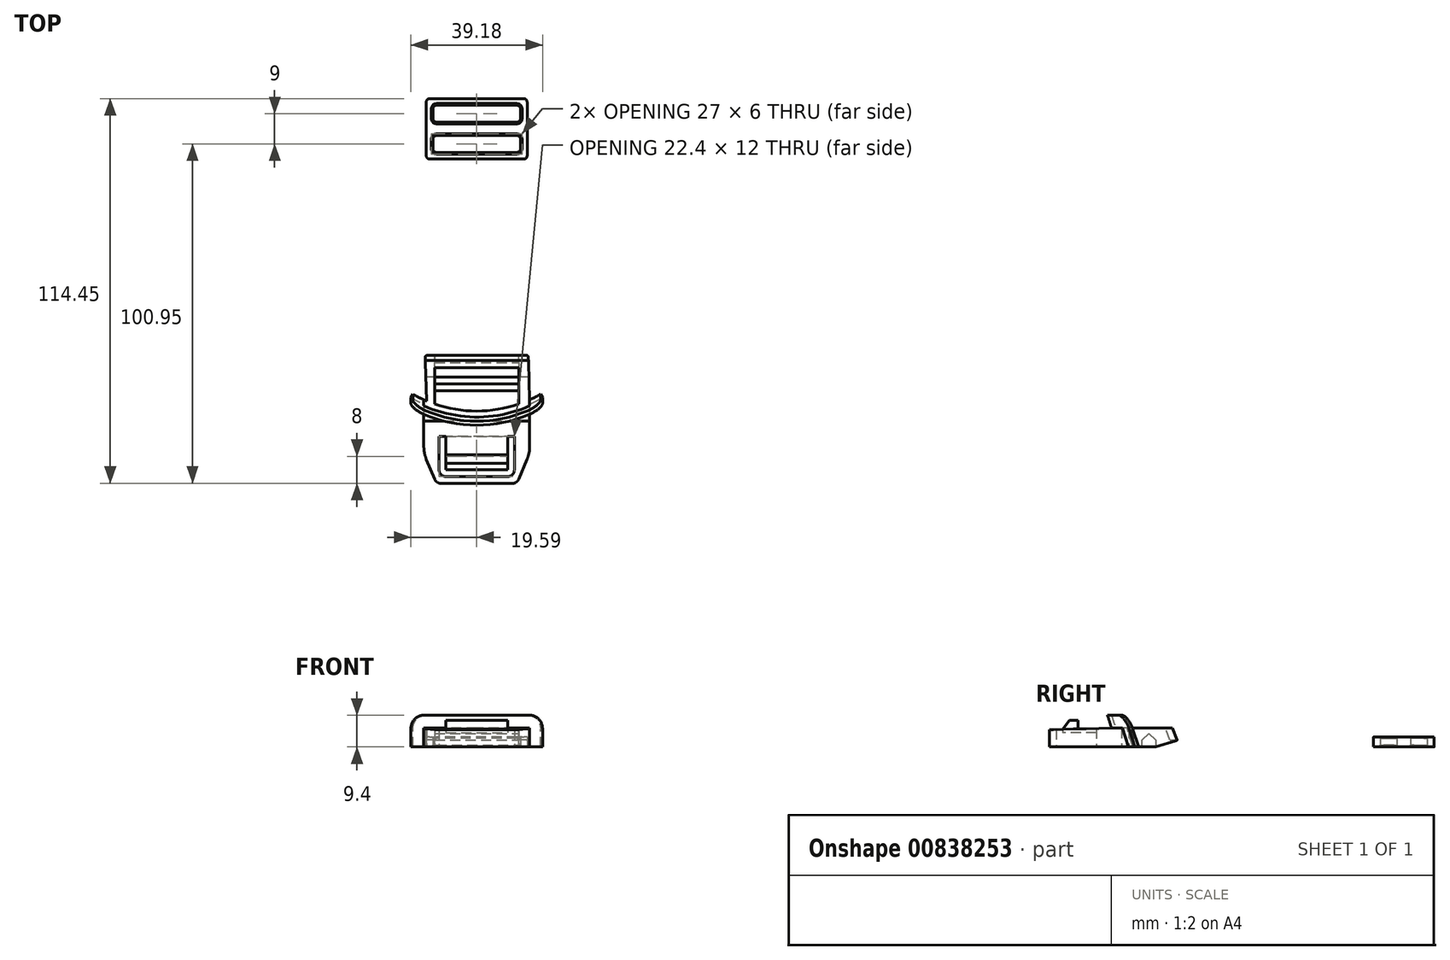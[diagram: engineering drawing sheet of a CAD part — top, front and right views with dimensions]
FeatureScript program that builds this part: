
annotation { "Feature Type Name" : "Feature", "Feature Type Description" : "" }
export const myFeature = defineFeature(function(context is Context, id is Id, definition is map)
    precondition{}
    {
        {
            var Q0;
            Q0=qCreatedBy(makeId("Top.planeOp"),FACE);
            var sketch = newSketch(context, id + "F0", { "sketchPlane" : qUnion([Q0])});
            skArc(sketch, "E0", {"start": v(-19, 0) * mm, "mid": v(0, -5) * mm, "end": v(19, 0) * mm});
            skLineSegment(sketch, "E1", {"start": v(0, 0) * mm, "end": v(0, -22.21) * mm, "construction": true});
            skLineSegment(sketch, "E2", {"start": v(-19, 0) * mm, "end": v(-19.6, -1.04) * mm});
            skArc(sketch, "E3", {"start": v(-19.6, -1.04) * mm, "mid": v(0, -6.2) * mm, "end": v(19.6, -1.04) * mm});
            skLineSegment(sketch, "E4", {"start": v(19, 0) * mm, "end": v(19.6, -1.04) * mm});
            skSolve(sketch);
        }
        {
            var Q0;
            Q0=qCreatedBy(makeId("Right.planeOp"),FACE);
            var sketch = newSketch(context, id + "F1", { "sketchPlane" : qUnion([Q0])});
            skLineSegment(sketch, "E5", {"start": v(-5, 0) * mm, "end": v(-8, 9.4) * mm});
            skSolve(sketch);
        }
        {
            var Q0;
            Q0=makeQuery(id+"F0.imprint","IMPRINT",FACE,{"disambiguationData":[TD([[makeQuery(id+"F0.imprint","IMPRINT",EDGE,{"derivedFrom":sQuery(id+"F0.wireOp",EDGE,"E0")}),-1.0]])]});
            var Q1;
            Q1=sQuery(id+"F1.wireOp",EDGE,"E5");
            sweep(context, id + "F2", {"profiles" : qUnion([Q0]), "path" : qUnion([Q1])});
        }
        {
            var Q0;
            Q0=qCreatedBy(makeId("Top.planeOp"),FACE);
            var sketch = newSketch(context, id + "F3", { "sketchPlane" : qUnion([Q0])});
            skLineSegment(sketch, "E6", {"start": v(-12, -26.5) * mm, "end": v(12, -26.5) * mm});
            skLineSegment(sketch, "E7", {"start": v(0, 0) * mm, "end": v(0, -12.9) * mm, "construction": true});
            skLineSegment(sketch, "E8", {"start": v(-15.75, -1.64) * mm, "end": v(-15.75, -17.5) * mm});
            skLineSegment(sketch, "E9", {"start": v(-15.75, -17.5) * mm, "end": v(-12, -26.5) * mm});
            skLineSegment(sketch, "E10.MirrorCS", {"start": v(15.75, -17.5) * mm, "end": v(12, -26.5) * mm});
            skLineSegment(sketch, "E11.MirrorCS", {"start": v(15.75, -1.64) * mm, "end": v(15.75, -17.5) * mm});
            skLineSegment(sketch, "E12", {"start": v(-11.2, -24.5) * mm, "end": v(-11.2, -12.5) * mm});
            skLineSegment(sketch, "E13", {"start": v(-11.2, -12.5) * mm, "end": v(-9.2, -12.5) * mm});
            skLineSegment(sketch, "E14", {"start": v(-9.2, -12.5) * mm, "end": v(-9.2, -22.5) * mm});
            skLineSegment(sketch, "E15", {"start": v(-9.2, -22.5) * mm, "end": v(9.2, -22.5) * mm});
            skLineSegment(sketch, "E16", {"start": v(-11.2, -24.5) * mm, "end": v(11.2, -24.5) * mm});
            skLineSegment(sketch, "E17.MirrorCS", {"start": v(11.2, -24.5) * mm, "end": v(11.2, -12.5) * mm});
            skLineSegment(sketch, "E18.MirrorCS", {"start": v(9.2, -12.5) * mm, "end": v(9.2, -22.5) * mm});
            skLineSegment(sketch, "E19.MirrorCS", {"start": v(11.2, -12.5) * mm, "end": v(9.2, -12.5) * mm});
            skArc(sketch, "E20.0", {"start": v(19, 0) * mm, "mid": v(0, -5) * mm, "end": v(-19, 0) * mm});
            skSolve(sketch);
        }
        {
            var Q0;
            Q0=makeQuery(id+"F3.imprint","IMPRINT",FACE,{"disambiguationData":[TD([[makeQuery(id+"F3.imprint","IMPRINT",EDGE,{"derivedFrom":sQuery(id+"F3.wireOp",EDGE,"E6")}),1.0]])]});
            extrude(context, id + "F4", {"entities" : qUnion([Q0]), "operationType" : NewBodyOperationType.ADD, "depth" : 5.6 * mm, "offsetDistance" : 25 * mm});
        }
        {
            var Q0;
            Q0=qCreatedBy(makeId("Right.planeOp"),FACE);
            var sketch = newSketch(context, id + "F5", { "sketchPlane" : qUnion([Q0])});
            skLineSegment(sketch, "E21", {"start": v(-7.99, 5.6) * mm, "end": v(-26.52, 5.1) * mm});
            skLineSegment(sketch, "E22", {"start": v(-26.5, 0) * mm, "end": v(-26.5, 5.6) * mm});
            skLineSegment(sketch, "E23", {"start": v(-26.5, 5.6) * mm, "end": v(-7.99, 5.6) * mm});
            skSolve(sketch);
        }
        {
            var Q0;
            {var subQ0=sQuery(id+"F5.wireOp",EDGE,"E23");Q0=makeQuery(id+"F5.imprint","IMPRINT",FACE,{"disambiguationData":[TD([[makeQuery(id+"F5.imprint","IMPRINT",EDGE,{"derivedFrom":subQ0}),-1.0]])]});}
            extrude(context, id + "F6", {"entities" : qUnion([Q0]), "operationType" : NewBodyOperationType.REMOVE, "endBound" : BoundingType.THROUGH_ALL, "oppositeDirection" : true, "depth" : 25 * mm, "offsetDistance" : 25 * mm, "hasSecondDirection" : true, "secondDirectionBound" : BoundingType.THROUGH_ALL, "secondDirectionOppositeDirection" : false, "secondDirectionDepth" : 25 * mm});
        }
        {
            var Q0;
            Q0=qCreatedBy(makeId("Right.planeOp"),FACE);
            var sketch = newSketch(context, id + "F7", { "sketchPlane" : qUnion([Q0])});
            skLineSegment(sketch, "E24", {"start": v(-22.5, 5.2) * mm, "end": v(-20.5, 7.86) * mm});
            skLineSegment(sketch, "E25", {"start": v(-20.5, 7.86) * mm, "end": v(-18, 7.93) * mm});
            skLineSegment(sketch, "E26", {"start": v(-18, 7.93) * mm, "end": v(-18, 5.33) * mm});
            skLineSegment(sketch, "E27", {"start": v(-18, 5.33) * mm, "end": v(-22.5, 5.2) * mm});
            skSolve(sketch);
        }
        {
            var Q0;
            Q0=makeQuery(id+"F7.imprint","IMPRINT",FACE,{"disambiguationData":[TD([[makeQuery(id+"F7.imprint","IMPRINT",EDGE,{"derivedFrom":sQuery(id+"F7.wireOp",EDGE,"E24")}),-1.0]])]});
            var Q1;
            Q1=makeQuery(id+"F4.opExtrude","SWEPT_FACE",FACE,{"disambiguationData":[OSD([sQuery(id+"F3.wireOp",EDGE,"E14")])]});
            var Q2;
            Q2=makeQuery(id+"F4.opExtrude","SWEPT_FACE",FACE,{"disambiguationData":[OSD([sQuery(id+"F3.wireOp",EDGE,"E18.MirrorCS")])]});
            extrude(context, id + "F8", {"entities" : qUnion([Q0]), "operationType" : NewBodyOperationType.ADD, "endBound" : BoundingType.UP_TO_SURFACE, "oppositeDirection" : true, "depth" : 25 * mm, "endBoundEntityFace" : qUnion([Q1]), "offsetDistance" : 25 * mm, "hasSecondDirection" : true, "secondDirectionBound" : BoundingType.UP_TO_SURFACE, "secondDirectionOppositeDirection" : false, "secondDirectionDepth" : 25 * mm, "secondDirectionBoundEntityFace" : qUnion([Q2])});
        }
        {
            var Q0;
            Q0=makeQuery(id+"F4.boolean.opBoolean","MERGE",FACE,{"derivedFrom":[makeQuery(id+"F2.opSweep","CAP_FACE",FACE,{"disambiguationData":[OSD([sQuery(id+"F0.wireOp",EDGE,"E0"),sQuery(id+"F0.wireOp",EDGE,"E2"),sQuery(id+"F0.wireOp",EDGE,"E3"),sQuery(id+"F0.wireOp",EDGE,"E4"),sQuery(id+"F1.wireOp",VERTEX,"E5.start")])],"isStart":true}),makeQuery(id+"F4.opExtrude","CAP_FACE",FACE,{"disambiguationData":[OSD([sQuery(id+"F3.wireOp",EDGE,"E6"),sQuery(id+"F3.wireOp",EDGE,"E8"),sQuery(id+"F3.wireOp",EDGE,"E9"),sQuery(id+"F3.wireOp",EDGE,"E10.MirrorCS"),sQuery(id+"F3.wireOp",EDGE,"E11.MirrorCS"),sQuery(id+"F3.wireOp",EDGE,"E12"),sQuery(id+"F3.wireOp",EDGE,"E13"),sQuery(id+"F3.wireOp",EDGE,"E14"),sQuery(id+"F3.wireOp",EDGE,"E15"),sQuery(id+"F3.wireOp",EDGE,"E16"),sQuery(id+"F3.wireOp",EDGE,"E17.MirrorCS"),sQuery(id+"F3.wireOp",EDGE,"E18.MirrorCS"),sQuery(id+"F3.wireOp",EDGE,"E19.MirrorCS"),sQuery(id+"F3.wireOp",EDGE,"E20.0")])],"isStart":true})]});
            var sketch = newSketch(context, id + "F9", { "sketchPlane" : qUnion([Q0])});
            skLineSegment(sketch, "E28", {"start": v(-9.2, 12.5) * mm, "end": v(9.2, 12.5) * mm});
            skSolve(sketch);
        }
        {
            var Q0;
            Q0=makeQuery(id+"F4.opExtrude","SWEPT_FACE",FACE,{"disambiguationData":[OSD([sQuery(id+"F3.wireOp",EDGE,"E15")])]});
            var sketch = newSketch(context, id + "F10", { "sketchPlane" : qUnion([Q0])});
            skPoint(sketch, "E29", {"position": v(-9.2, 4.2) * mm});
            skSolve(sketch);
        }
        {
            var Q0;
            Q0=makeQuery(id+"F9.imprint","IMPRINT",FACE,{"disambiguationData":[TD([[makeQuery(id+"F9.imprint","IMPRINT",EDGE,{"derivedFrom":sQuery(id+"F9.wireOp",EDGE,"E28")}),1.0]])]});
            var Q1;
            Q1=sQuery(id+"F10.wireOp",VERTEX,"E29");
            extrude(context, id + "F11", {"entities" : qUnion([Q0]), "operationType" : NewBodyOperationType.REMOVE, "endBound" : BoundingType.UP_TO_VERTEX, "oppositeDirection" : true, "depth" : 25 * mm, "endBoundEntityVertex" : qUnion([Q1]), "offsetDistance" : 25 * mm});
        }
        {
            var Q0;
            Q0=qCreatedBy(makeId("Top.planeOp"),FACE);
            var sketch = newSketch(context, id + "F12", { "sketchPlane" : qUnion([Q0])});
            skLineSegment(sketch, "E30.bottom", {"start": v(-12.5, 12.04) * mm, "end": v(12.5, 12.04) * mm});
            skLineSegment(sketch, "E30.left", {"start": v(-12.5, 12.04) * mm, "end": v(-12.5, -2.95) * mm});
            skLineSegment(sketch, "E30.right", {"start": v(12.5, 12.04) * mm, "end": v(12.5, -2.95) * mm});
            skLineSegment(sketch, "E31.bottom", {"start": v(-15.32, 12.04) * mm, "end": v(15.32, 12.04) * mm});
            skLineSegment(sketch, "E31.top", {"start": v(-14.9, -2.95) * mm, "end": v(15.75, -2.95) * mm});
            skLineSegment(sketch, "E31.left", {"start": v(-15.32, 12.04) * mm, "end": v(-14.9, -2.95) * mm});
            skLineSegment(sketch, "E31.right", {"start": v(15.32, 12.04) * mm, "end": v(15.75, -2.95) * mm});
            skSolve(sketch);
        }
        {
            var Q0;
            {var subQ0=sQuery(id+"F12.wireOp",EDGE,"E30.left");Q0=makeQuery(id+"F12.imprint","IMPRINT",FACE,{"disambiguationData":[TD([[makeQuery(id+"F12.imprint","IMPRINT",EDGE,{"derivedFrom":subQ0}),-1.0]])]});}
            var Q1;
            {var subQ0=sQuery(id+"F12.wireOp",EDGE,"E30.right");Q1=makeQuery(id+"F12.imprint","IMPRINT",FACE,{"disambiguationData":[TD([[makeQuery(id+"F12.imprint","IMPRINT",EDGE,{"derivedFrom":subQ0}),1.0]])]});}
            var Q2;
            {var subQ0=sQuery(id+"F3.wireOp",EDGE,"E8");var subQ1=sQuery(id+"F3.wireOp",EDGE,"E11.MirrorCS");var subQ2=sQuery(id+"F3.wireOp",EDGE,"E20.0");Q2=makeQuery(id+"F4.boolean.opBoolean","SPLIT",FACE,{"disambiguationData":[TD([makeQuery(id+"F4.opExtrude","SWEPT_FACE",FACE,{"disambiguationData":[OSD([subQ2])]})])],"derivedFrom":makeQuery(id+"F4.opExtrude","CAP_FACE",FACE,{"disambiguationData":[OSD([sQuery(id+"F3.wireOp",EDGE,"E6"),subQ0,sQuery(id+"F3.wireOp",EDGE,"E9"),sQuery(id+"F3.wireOp",EDGE,"E10.MirrorCS"),subQ1,sQuery(id+"F3.wireOp",EDGE,"E12"),sQuery(id+"F3.wireOp",EDGE,"E13"),sQuery(id+"F3.wireOp",EDGE,"E14"),sQuery(id+"F3.wireOp",EDGE,"E15"),sQuery(id+"F3.wireOp",EDGE,"E16"),sQuery(id+"F3.wireOp",EDGE,"E17.MirrorCS"),sQuery(id+"F3.wireOp",EDGE,"E18.MirrorCS"),sQuery(id+"F3.wireOp",EDGE,"E19.MirrorCS"),subQ2])],"isStart":false})});}
            extrude(context, id + "F13", {"entities" : qUnion([Q0, Q1]), "operationType" : NewBodyOperationType.ADD, "endBound" : BoundingType.UP_TO_SURFACE, "depth" : 25 * mm, "endBoundEntityFace" : qUnion([Q2]), "offsetDistance" : 25 * mm});
        }
        {
            var Q0;
            Q0=makeQuery(id+"F13.opExtrude","SWEPT_FACE",FACE,{"disambiguationData":[OSD([sQuery(id+"F12.wireOp",EDGE,"E30.right")])]});
            var sketch = newSketch(context, id + "F14", { "sketchPlane" : qUnion([Q0])});
            skLineSegment(sketch, "E32", {"start": v(-1.08, 0) * mm, "end": v(-1.08, 2) * mm});
            skLineSegment(sketch, "E33", {"start": v(-1.08, 2) * mm, "end": v(-3.08, 4) * mm});
            skLineSegment(sketch, "E34", {"start": v(-3.08, 4) * mm, "end": v(-5.08, 2) * mm});
            skLineSegment(sketch, "E35", {"start": v(-5.08, 2) * mm, "end": v(-5.08, 0) * mm});
            skLineSegment(sketch, "E36", {"start": v(-3.08, 0) * mm, "end": v(-3.08, 4) * mm, "construction": true});
            skLineSegment(sketch, "E37", {"start": v(-9.4, 2) * mm, "end": v(-7.94, 5.6) * mm});
            skLineSegment(sketch, "E38", {"start": v(-7.94, 5.6) * mm, "end": v(-10.1, 5.6) * mm});
            skLineSegment(sketch, "E39", {"start": v(-10.1, 5.6) * mm, "end": v(-11.55, 2) * mm});
            skLineSegment(sketch, "E40", {"start": v(-9.4, 2) * mm, "end": v(-11.55, 2) * mm});
            skLineSegment(sketch, "E41", {"start": v(-11.55, 2) * mm, "end": v(-5.08, 0) * mm});
            skSolve(sketch);
        }
        {
            var Q0;
            {var subQ1=sQuery(id+"F14.wireOp",EDGE,"E32");Q0=makeQuery(id+"F14.imprint","IMPRINT",FACE,{"disambiguationData":[TD([[makeQuery(id+"F14.imprint","IMPRINT",EDGE,{"derivedFrom":subQ1}),1.0]])]});}
            var Q1;
            {var subQ0=sQuery(id+"F14.wireOp",EDGE,"E37");Q1=makeQuery(id+"F14.imprint","IMPRINT",FACE,{"disambiguationData":[TD([[makeQuery(id+"F14.imprint","IMPRINT",EDGE,{"derivedFrom":subQ0}),1.0]])]});}
            var Q2;
            Q2=makeQuery(id+"F13.opExtrude","SWEPT_FACE",FACE,{"disambiguationData":[OSD([sQuery(id+"F12.wireOp",EDGE,"E30.left")])]});
            extrude(context, id + "F15", {"entities" : qUnion([Q0, Q1]), "operationType" : NewBodyOperationType.ADD, "endBound" : BoundingType.UP_TO_SURFACE, "depth" : 25 * mm, "endBoundEntityFace" : qUnion([Q2]), "offsetDistance" : 25 * mm});
        }
        {
            var Q0;
            {var subQ4=sQuery(id+"F14.wireOp",EDGE,"E39");Q0=makeQuery(id+"F14.imprint","IMPRINT",FACE,{"disambiguationData":[TD([[makeQuery(id+"F14.imprint","IMPRINT",EDGE,{"derivedFrom":subQ4}),-1.0]])]});}
            extrude(context, id + "F16", {"entities" : qUnion([Q0]), "operationType" : NewBodyOperationType.REMOVE, "endBound" : BoundingType.THROUGH_ALL, "oppositeDirection" : true, "depth" : 25 * mm, "offsetDistance" : 25 * mm, "hasSecondDirection" : true, "secondDirectionBound" : BoundingType.THROUGH_ALL, "secondDirectionOppositeDirection" : false, "secondDirectionDepth" : 25 * mm});
        }
        {
            var Q0;
            Q0=makeQuery(id+"F4.opExtrude","SWEPT_EDGE",EDGE,{"disambiguationData":[OSD([sQuery(id+"F3.wireOp",EDGE,"E12"),sQuery(id+"F3.wireOp",EDGE,"E16")])]});
            var Q1;
            Q1=makeQuery(id+"F4.opExtrude","SWEPT_EDGE",EDGE,{"disambiguationData":[OSD([sQuery(id+"F3.wireOp",EDGE,"E16"),sQuery(id+"F3.wireOp",EDGE,"E17.MirrorCS")])]});
            var Q2;
            Q2=makeQuery(id+"F4.opExtrude","SWEPT_EDGE",EDGE,{"disambiguationData":[OSD([sQuery(id+"F3.wireOp",EDGE,"E6"),sQuery(id+"F3.wireOp",EDGE,"E9")])]});
            var Q3;
            Q3=makeQuery(id+"F4.opExtrude","SWEPT_EDGE",EDGE,{"disambiguationData":[OSD([sQuery(id+"F3.wireOp",EDGE,"E6"),sQuery(id+"F3.wireOp",EDGE,"E10.MirrorCS")])]});
            fillet(context, id + "F17", {"entities" : qUnion([Q0, Q1, Q2, Q3]), "radius" : 2 * mm, "tangentPropagation" : true, "allowEdgeOverflow" : false});
        }
        {
            var Q0;
            Q0=makeQuery(id+"F4.opExtrude","SWEPT_EDGE",EDGE,{"disambiguationData":[OSD([sQuery(id+"F3.wireOp",EDGE,"E10.MirrorCS"),sQuery(id+"F3.wireOp",EDGE,"E11.MirrorCS")])]});
            var Q1;
            Q1=makeQuery(id+"F4.opExtrude","SWEPT_EDGE",EDGE,{"disambiguationData":[OSD([sQuery(id+"F3.wireOp",EDGE,"E8"),sQuery(id+"F3.wireOp",EDGE,"E9")])]});
            fillet(context, id + "F18", {"entities" : qUnion([Q0, Q1]), "radius" : 10 * mm, "tangentPropagation" : true, "allowEdgeOverflow" : false});
        }
        {
            var Q0;
            Q0=makeQuery(id+"F2.opSweep","CAP_EDGE",EDGE,{"disambiguationData":[OSD([sQuery(id+"F0.wireOp",EDGE,"E2"),sQuery(id+"F1.wireOp",VERTEX,"E5.end")])],"isStart":false});
            var Q1;
            Q1=makeQuery(id+"F2.opSweep","CAP_EDGE",EDGE,{"disambiguationData":[OSD([sQuery(id+"F0.wireOp",EDGE,"E4"),sQuery(id+"F1.wireOp",VERTEX,"E5.end")])],"isStart":false});
            fillet(context, id + "F19", {"entities" : qUnion([Q0, Q1]), "radius" : 5 * mm, "tangentPropagation" : true, "allowEdgeOverflow" : false});
        }
        {
            var Q0;
            Q0=makeQuery(id+"F16.boolean.opBoolean","INTERSECT",EDGE,{"derivedFrom":[makeQuery(id+"F13.opExtrude","SWEPT_FACE",FACE,{"disambiguationData":[OSD([sQuery(id+"F12.wireOp",EDGE,"E31.left")])]}),makeQuery(id+"F16.opExtrude","SWEPT_FACE",FACE,{"disambiguationData":[OSD([sQuery(id+"F14.wireOp",EDGE,"E39")])]})]});
            var Q1;
            Q1=makeQuery(id+"F16.boolean.opBoolean","INTERSECT",EDGE,{"derivedFrom":[makeQuery(id+"F13.opExtrude","SWEPT_FACE",FACE,{"disambiguationData":[OSD([sQuery(id+"F12.wireOp",EDGE,"E31.right")])]}),makeQuery(id+"F16.opExtrude","SWEPT_FACE",FACE,{"disambiguationData":[OSD([sQuery(id+"F14.wireOp",EDGE,"E39")])]})]});
            var Q2;
            Q2=makeQuery(id+"F15.opExtrude","TWEAK_EDGE",EDGE,{"derivedFrom":[makeQuery(id+"F13.opExtrude","SWEPT_FACE",FACE,{"disambiguationData":[OSD([sQuery(id+"F12.wireOp",EDGE,"E30.left")])]}),makeQuery(id+"F14.imprint","IMPRINT",EDGE,{"derivedFrom":sQuery(id+"F14.wireOp",EDGE,"E37")})]});
            fillet(context, id + "F20", {"entities" : qUnion([Q0, Q1, Q2]), "radius" : 0.5 * mm, "tangentPropagation" : true, "allowEdgeOverflow" : false});
        }
        {
            var Q0;
            Q0=qCreatedBy(makeId("Top.planeOp"),FACE);
            var sketch = newSketch(context, id + "F21", { "sketchPlane" : qUnion([Q0])});
            skLineSegment(sketch, "E42.bottom", {"start": v(-15, 87.95) * mm, "end": v(15, 87.95) * mm});
            skLineSegment(sketch, "E42.top", {"start": v(-15, 69.95) * mm, "end": v(15, 69.95) * mm});
            skLineSegment(sketch, "E42.left", {"start": v(-15, 87.95) * mm, "end": v(-15, 69.95) * mm});
            skLineSegment(sketch, "E42.right", {"start": v(15, 87.95) * mm, "end": v(15, 69.95) * mm});
            skPoint(sketch, "E42.middle", {"position": v(0, 78.95) * mm});
            skLineSegment(sketch, "E43.bottom", {"start": v(-13, 85.95) * mm, "end": v(13, 85.95) * mm});
            skLineSegment(sketch, "E43.top", {"start": v(-13, 80.95) * mm, "end": v(13, 80.95) * mm});
            skLineSegment(sketch, "E43.left", {"start": v(-13, 85.95) * mm, "end": v(-13, 80.95) * mm});
            skLineSegment(sketch, "E43.right", {"start": v(13, 85.95) * mm, "end": v(13, 80.95) * mm});
            skPoint(sketch, "E43.middle", {"position": v(0, 83.45) * mm});
            skLineSegment(sketch, "E44", {"start": v(-15, 78.95) * mm, "end": v(15, 78.95) * mm, "construction": true});
            skLineSegment(sketch, "E45.MirrorCS", {"start": v(-13, 71.95) * mm, "end": v(13, 71.95) * mm});
            skLineSegment(sketch, "E46.MirrorCS", {"start": v(-13, 76.95) * mm, "end": v(13, 76.95) * mm});
            skLineSegment(sketch, "E47.MirrorCS", {"start": v(13, 71.95) * mm, "end": v(13, 76.95) * mm});
            skLineSegment(sketch, "E48.MirrorCS", {"start": v(-13, 71.95) * mm, "end": v(-13, 76.95) * mm});
            skSolve(sketch);
        }
        {
            var Q0;
            Q0=makeQuery(id+"F21.imprint","IMPRINT",FACE,{"disambiguationData":[TD([[makeQuery(id+"F21.imprint","IMPRINT",EDGE,{"derivedFrom":sQuery(id+"F21.wireOp",EDGE,"E42.bottom")}),-1.0]])]});
            extrude(context, id + "F22", {"entities" : qUnion([Q0]), "depth" : 3 * mm, "offsetDistance" : 25 * mm});
        }
        {
            var Q0;
            Q0=makeQuery(id+"F22.opExtrude","SWEPT_EDGE",EDGE,{"disambiguationData":[OSD([sQuery(id+"F21.wireOp",EDGE,"E43.bottom"),sQuery(id+"F21.wireOp",EDGE,"E43.left")])]});
            var Q1;
            Q1=makeQuery(id+"F22.opExtrude","SWEPT_EDGE",EDGE,{"disambiguationData":[OSD([sQuery(id+"F21.wireOp",EDGE,"E43.bottom"),sQuery(id+"F21.wireOp",EDGE,"E43.right")])]});
            var Q2;
            Q2=makeQuery(id+"F22.opExtrude","SWEPT_EDGE",EDGE,{"disambiguationData":[OSD([sQuery(id+"F21.wireOp",EDGE,"E46.MirrorCS"),sQuery(id+"F21.wireOp",EDGE,"E48.MirrorCS")])]});
            var Q3;
            Q3=makeQuery(id+"F22.opExtrude","SWEPT_EDGE",EDGE,{"disambiguationData":[OSD([sQuery(id+"F21.wireOp",EDGE,"E45.MirrorCS"),sQuery(id+"F21.wireOp",EDGE,"E48.MirrorCS")])]});
            var Q4;
            Q4=makeQuery(id+"F22.opExtrude","SWEPT_EDGE",EDGE,{"disambiguationData":[OSD([sQuery(id+"F21.wireOp",EDGE,"E45.MirrorCS"),sQuery(id+"F21.wireOp",EDGE,"E47.MirrorCS")])]});
            var Q5;
            Q5=makeQuery(id+"F22.opExtrude","SWEPT_EDGE",EDGE,{"disambiguationData":[OSD([sQuery(id+"F21.wireOp",EDGE,"E46.MirrorCS"),sQuery(id+"F21.wireOp",EDGE,"E47.MirrorCS")])]});
            var Q6;
            Q6=makeQuery(id+"F22.opExtrude","SWEPT_EDGE",EDGE,{"disambiguationData":[OSD([sQuery(id+"F21.wireOp",EDGE,"E42.top"),sQuery(id+"F21.wireOp",EDGE,"E42.right")])]});
            var Q7;
            Q7=makeQuery(id+"F22.opExtrude","SWEPT_EDGE",EDGE,{"disambiguationData":[OSD([sQuery(id+"F21.wireOp",EDGE,"E42.top"),sQuery(id+"F21.wireOp",EDGE,"E42.left")])]});
            var Q8;
            Q8=makeQuery(id+"F22.opExtrude","SWEPT_EDGE",EDGE,{"disambiguationData":[OSD([sQuery(id+"F21.wireOp",EDGE,"E42.bottom"),sQuery(id+"F21.wireOp",EDGE,"E42.left")])]});
            var Q9;
            Q9=makeQuery(id+"F22.opExtrude","SWEPT_EDGE",EDGE,{"disambiguationData":[OSD([sQuery(id+"F21.wireOp",EDGE,"E43.top"),sQuery(id+"F21.wireOp",EDGE,"E43.right")])]});
            var Q10;
            Q10=makeQuery(id+"F22.opExtrude","SWEPT_EDGE",EDGE,{"disambiguationData":[OSD([sQuery(id+"F21.wireOp",EDGE,"E43.top"),sQuery(id+"F21.wireOp",EDGE,"E43.left")])]});
            var Q11;
            Q11=makeQuery(id+"F22.opExtrude","SWEPT_EDGE",EDGE,{"disambiguationData":[OSD([sQuery(id+"F21.wireOp",EDGE,"E42.bottom"),sQuery(id+"F21.wireOp",EDGE,"E42.right")])]});
            fillet(context, id + "F23", {"entities" : qUnion([Q0, Q1, Q2, Q3, Q4, Q5, Q6, Q7, Q8, Q9, Q10, Q11]), "radius" : 1 * mm, "tangentPropagation" : true, "allowEdgeOverflow" : false});
        }
        {
            var Q0;
            Q0=makeQuery(id+"F22.opExtrude","CAP_EDGE",EDGE,{"disambiguationData":[OSD([sQuery(id+"F21.wireOp",EDGE,"E43.top")])],"isStart":false});
            var Q1;
            Q1=makeQuery(id+"F22.opExtrude","CAP_EDGE",EDGE,{"disambiguationData":[OSD([sQuery(id+"F21.wireOp",EDGE,"E43.left")])],"isStart":false});
            var Q2;
            {var subQ0=sQuery(id+"F21.wireOp",EDGE,"E43.left");var subQ1=sQuery(id+"F21.wireOp",EDGE,"E43.bottom");Q2=makeQuery(id+"F23.opFillet","BLEND_EDGE",EDGE,{"blendedFrom":[makeQuery(id+"F22.opExtrude","SWEPT_EDGE",EDGE,{"disambiguationData":[OSD([subQ1,subQ0])]}),makeQuery(id+"F22.opExtrude","CAP_FACE",FACE,{"disambiguationData":[OSD([sQuery(id+"F21.wireOp",EDGE,"E42.bottom"),sQuery(id+"F21.wireOp",EDGE,"E42.top"),sQuery(id+"F21.wireOp",EDGE,"E42.left"),sQuery(id+"F21.wireOp",EDGE,"E42.right"),subQ1,sQuery(id+"F21.wireOp",EDGE,"E43.top"),subQ0,sQuery(id+"F21.wireOp",EDGE,"E43.right"),sQuery(id+"F21.wireOp",EDGE,"E46.MirrorCS"),sQuery(id+"F21.wireOp",EDGE,"E45.MirrorCS"),sQuery(id+"F21.wireOp",EDGE,"E47.MirrorCS"),sQuery(id+"F21.wireOp",EDGE,"E48.MirrorCS")])],"isStart":false})],"blendedInto":[makeQuery(id+"F22.opExtrude","CAP_FACE",FACE,{"disambiguationData":[OSD([sQuery(id+"F21.wireOp",EDGE,"E42.bottom"),sQuery(id+"F21.wireOp",EDGE,"E42.top"),sQuery(id+"F21.wireOp",EDGE,"E42.left"),sQuery(id+"F21.wireOp",EDGE,"E42.right"),subQ1,sQuery(id+"F21.wireOp",EDGE,"E43.top"),subQ0,sQuery(id+"F21.wireOp",EDGE,"E43.right"),sQuery(id+"F21.wireOp",EDGE,"E46.MirrorCS"),sQuery(id+"F21.wireOp",EDGE,"E45.MirrorCS"),sQuery(id+"F21.wireOp",EDGE,"E47.MirrorCS"),sQuery(id+"F21.wireOp",EDGE,"E48.MirrorCS")])],"isStart":false})]});}
            var Q3;
            Q3=makeQuery(id+"F22.opExtrude","CAP_EDGE",EDGE,{"disambiguationData":[OSD([sQuery(id+"F21.wireOp",EDGE,"E46.MirrorCS")])],"isStart":false});
            var Q4;
            Q4=makeQuery(id+"F22.opExtrude","CAP_EDGE",EDGE,{"disambiguationData":[OSD([sQuery(id+"F21.wireOp",EDGE,"E46.MirrorCS")])],"isStart":true});
            var Q5;
            Q5=makeQuery(id+"F22.opExtrude","CAP_EDGE",EDGE,{"disambiguationData":[OSD([sQuery(id+"F21.wireOp",EDGE,"E43.top")])],"isStart":true});
            chamfer(context, id + "F24", {"entities" : qUnion([Q0, Q1, Q2, Q3, Q4, Q5]), "width" : 0.5 * mm, "tangentPropagation" : true});
        }
    });
